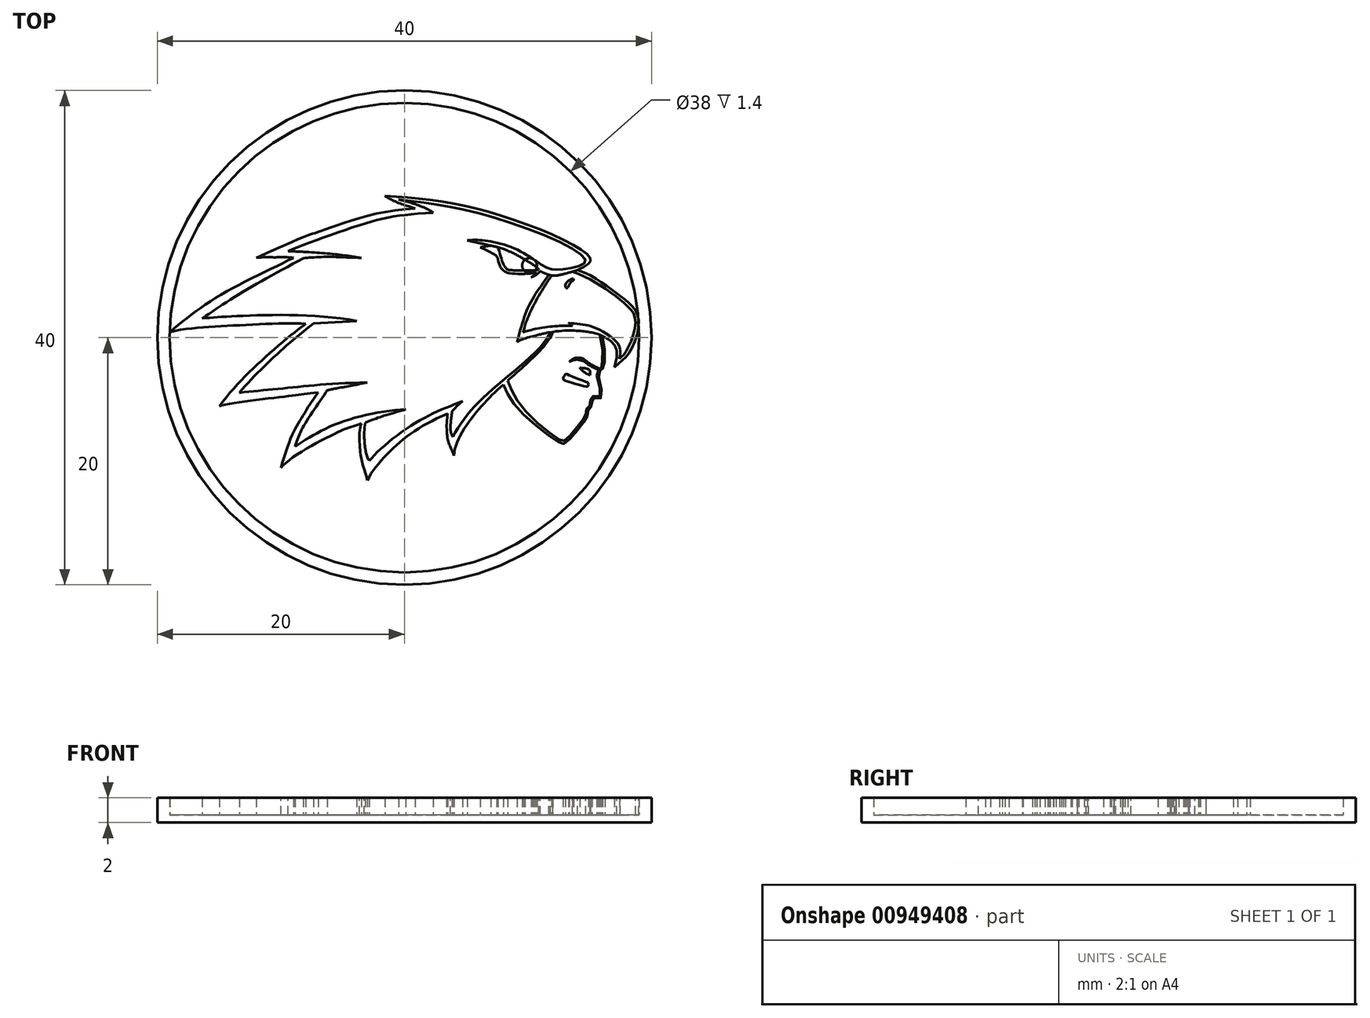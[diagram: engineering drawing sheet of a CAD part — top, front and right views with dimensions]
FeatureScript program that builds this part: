
annotation { "Feature Type Name" : "Feature", "Feature Type Description" : "" }
export const myFeature = defineFeature(function(context is Context, id is Id, definition is map)
    precondition{}
    {
        {
            var Q0;
            Q0=qCreatedBy(makeId("Top.planeOp"),FACE);
            var sketch = newSketch(context, id + "F0", { "sketchPlane" : qUnion([Q0])});
            skCircle(sketch, "E0", {"center": v(0, 0) * mm, "radius": 20 * mm});
            skSolve(sketch);
        }
        {
            var Q0;
            Q0=makeQuery(id+"F0.imprint","IMPRINT",FACE,{"disambiguationData":[TD([[makeQuery(id+"F0.imprint","IMPRINT",EDGE,{"derivedFrom":sQuery(id+"F0.wireOp",EDGE,"E0")}),1.0]])]});
            extrude(context, id + "F1", {"entities" : qUnion([Q0]), "oppositeDirection" : true, "depth" : 0.6 * mm, "offsetDistance" : 25 * mm});
        }
        {
            var Q0;
            Q0=qCreatedBy(makeId("Top.planeOp"),FACE);
            var sketch = newSketch(context, id + "F2", { "sketchPlane" : qUnion([Q0])});
            skCircle(sketch, "E1", {"center": v(0, 0) * mm, "radius": 20 * mm});
            skCircle(sketch, "E2", {"center": v(0, 0) * mm, "radius": 19 * mm});
            skSolve(sketch);
        }
        {
            var Q0;
            Q0=makeQuery(id+"F2.imprint","IMPRINT",FACE,{"disambiguationData":[TD([[makeQuery(id+"F2.imprint","IMPRINT",EDGE,{"derivedFrom":sQuery(id+"F2.wireOp",EDGE,"E1")}),1.0]])]});
            extrude(context, id + "F3", {"entities" : qUnion([Q0]), "operationType" : NewBodyOperationType.ADD, "depth" : 1.4 * mm, "offsetDistance" : 25 * mm});
        }
        {
            var Q0;
            Q0=qCreatedBy(makeId("Top.planeOp"),FACE);
            var sketch = newSketch(context, id + "F4", { "sketchPlane" : qUnion([Q0])});
            skFitSpline(sketch, "E3", {"points": [v(-1.58, 11.46) * mm, v(7.72, 9.91) * mm, v(15.05, 6.42) * mm, v(14, 5.46) * mm], "startDerivative": vector(21.52, -1.26) * mm, "endDerivative": vector(-13.3, -6.93) * mm});
            skFitSpline(sketch, "E4", {"points": [v(3.5, -6.16) * mm, v(-0.78, -8.83) * mm, v(-3, -11.54) * mm], "startDerivative": vector(-10.76, -4.46) * mm, "endDerivative": vector(-2.73, -5.76) * mm});
            skFitSpline(sketch, "E5", {"points": [v(-3, -11.54) * mm, v(-3.55, -9.5) * mm, v(-3.5, -6.96) * mm], "startDerivative": vector(-2.35, 7.78) * mm, "endDerivative": vector(1.35, 3.27) * mm});
            skFitSpline(sketch, "E6", {"points": [v(-3.5, -6.96) * mm, v(-5.27, -7.6) * mm, v(-10, -10.54) * mm], "startDerivative": vector(-9.15, -3.1) * mm, "endDerivative": vector(-2.97, -4.21) * mm});
            skFitSpline(sketch, "E7", {"points": [v(-10, -10.54) * mm, v(-8.32, -6.48) * mm, v(-7, -4.44) * mm], "startDerivative": vector(3.25, 11.93) * mm, "endDerivative": vector(2.66, 3.7) * mm});
            skFitSpline(sketch, "E8", {"points": [v(-7, -4.44) * mm, v(-9.47, -4.75) * mm, v(-15, -5.54) * mm], "startDerivative": vector(-8.24, -0.84) * mm, "endDerivative": vector(-4.12, -1.43) * mm});
            skFitSpline(sketch, "E9", {"points": [v(-15, -5.54) * mm, v(-11, -1.34) * mm, v(-8, 1.1) * mm], "startDerivative": vector(6.54, 8.64) * mm, "endDerivative": vector(3.53, 2.33) * mm});
            skFitSpline(sketch, "E10", {"points": [v(-8, 1.1) * mm, v(-13.7, 0.98) * mm, v(-19, 0.46) * mm], "startDerivative": vector(-8.4, 0.77) * mm, "endDerivative": vector(-10.04, -2.22) * mm});
            skFitSpline(sketch, "E11", {"points": [v(-19, 0.46) * mm, v(-14.13, 3.88) * mm, v(-8, 7.06) * mm], "startDerivative": vector(8.8, 7.31) * mm, "endDerivative": vector(6.6, 4.65) * mm});
            skFitSpline(sketch, "E12", {"points": [v(-12, 6.46) * mm, v(-6.88, 8.58) * mm, v(0.86, 10.46) * mm], "startDerivative": vector(30.08, 13.67) * mm, "endDerivative": vector(18.85, 0.85) * mm});
            skFitSpline(sketch, "E13", {"points": [v(0.86, 10.46) * mm, v(-0.78, 11.03) * mm, v(-1.58, 11.46) * mm], "startDerivative": vector(-2.07, 0.66) * mm, "endDerivative": vector(-0.97, 0.57) * mm});
            skFitSpline(sketch, "E14", {"points": [v(3.5, -6.16) * mm, v(3.53, -8.34) * mm, v(4, -9.54) * mm], "startDerivative": vector(-0.77, -3.97) * mm, "endDerivative": vector(1.6, -4.4) * mm});
            skFitSpline(sketch, "E15", {"points": [v(4, -9.54) * mm, v(5.91, -5.93) * mm, v(9.09, -2.82) * mm, v(12, 0.46) * mm], "startDerivative": vector(0.54, 10.48) * mm, "endDerivative": vector(2.95, 8.84) * mm});
            skFitSpline(sketch, "E16", {"points": [v(-9, 6.46) * mm, v(-10.52, 6.5) * mm, v(-12, 6.46) * mm], "startDerivative": vector(-3.14, 0.42) * mm, "endDerivative": vector(-2.86, -0.43) * mm});
            skFitSpline(sketch, "E17", {"points": [v(14, 5.46) * mm, v(16.43, 4.12) * mm, v(18.07, 2.88) * mm, v(18.94, 1.52) * mm, v(18.18, -1.26) * mm, v(17, -2.4) * mm], "startDerivative": vector(12.4, -3.48) * mm, "endDerivative": vector(-8.18, -8.07) * mm});
            skFitSpline(sketch, "E18", {"points": [v(17, -2.4) * mm, v(17.07, -0.75) * mm, v(15.73, 0.25) * mm, v(14.63, 0.5) * mm, v(12, 0.46) * mm], "startDerivative": vector(1.76, 6.26) * mm, "endDerivative": vector(-11.27, -1.86) * mm});
            skFitSpline(sketch, "E19", {"points": [v(11, 5.38) * mm, v(9.78, 6.3) * mm, v(7, 7.43) * mm], "startDerivative": vector(-2.8, 3.17) * mm, "endDerivative": vector(-5.7, 0.83) * mm});
            skFitSpline(sketch, "E20", {"points": [v(7, 7.43) * mm, v(7.74, 5.78) * mm, v(8, 5.43) * mm, v(8.44, 5.22) * mm, v(10.45, 5.2) * mm, v(10.9, 5.29) * mm, v(11, 5.38) * mm], "startDerivative": vector(6.03, -7.57) * mm, "endDerivative": vector(2.14, 2.82) * mm});
            skCircle(sketch, "E21", {"center": v(10.12, 5.84) * mm, "radius": 0.6 * mm});
            skFitSpline(sketch, "E22", {"points": [v(8, -3.8) * mm, v(9.3, -5.87) * mm, v(12.45, -8.44) * mm, v(13, -8.54) * mm, v(14.33, -7.05) * mm, v(14.82, -6.23) * mm, v(14.93, -5.76) * mm, v(15.19, -5.5) * mm, v(15.2, -4.92) * mm, v(15.93, -4.86) * mm, v(15.7, -2.86) * mm, v(15.92, -2.64) * mm, v(16.1, -2.38) * mm, v(16, 0.14) * mm], "startDerivative": vector(7.5, -17.46) * mm, "endDerivative": vector(-8.07, 26.27) * mm});
            skFitSpline(sketch, "E23", {"points": [v(15.02, -3.03) * mm, v(14.56, -2.8) * mm, v(14.2, -2.44) * mm], "startDerivative": vector(-1.12, 0.33) * mm, "endDerivative": vector(-0.33, 0.79) * mm});
            skFitSpline(sketch, "E24", {"points": [v(14.2, -2.44) * mm, v(14.57, -2.47) * mm, v(14.94, -2.61) * mm, v(15.04, -2.8) * mm, v(15.02, -3.03) * mm], "startDerivative": vector(1.37, -0.38) * mm, "endDerivative": vector(-0.15, -0.97) * mm});
            skFitSpline(sketch, "E25", {"points": [v(15.68, -2.55) * mm, v(15.48, -2.5) * mm, v(14.93, -2.22) * mm, v(14.67, -2.02) * mm, v(14.03, -1.79) * mm, v(13.34, -1.95) * mm], "startDerivative": vector(-2.24, 0.34) * mm, "endDerivative": vector(-2.61, -1.2) * mm});
            skFitSpline(sketch, "E26", {"points": [v(13.34, -1.95) * mm, v(13.86, -1.65) * mm, v(14.3, -1.65) * mm, v(14.57, -1.77) * mm, v(15.07, -2.15) * mm, v(15.55, -2.4) * mm, v(15.89, -2.49) * mm], "startDerivative": vector(2.26, 2.4) * mm, "endDerivative": vector(2.1, 0.6) * mm});
            skFitSpline(sketch, "E27", {"points": [v(15.68, -2.55) * mm, v(15.8, -2.54) * mm, v(15.89, -2.49) * mm], "startDerivative": vector(0.25, -0.06) * mm, "endDerivative": vector(0.25, 0.3) * mm});
            skFitSpline(sketch, "E28", {"points": [v(14.52, -3.93) * mm, v(12.97, -3.46) * mm, v(12.85, -3.33) * mm, v(12.9, -3.2) * mm, v(12.98, -3) * mm, v(13.07, -2.94) * mm, v(13.22, -3) * mm, v(14.68, -3.57) * mm, v(14.86, -3.66) * mm, v(14.9, -3.76) * mm, v(14.84, -3.93) * mm, v(14.78, -3.97) * mm, v(14.52, -3.93) * mm]});
            skFitSpline(sketch, "E29", {"points": [v(12, 0.46) * mm, v(10.73, 0.2) * mm, v(9.12, -0.4) * mm], "startDerivative": vector(-4.79, -0.65) * mm, "endDerivative": vector(-1.75, -1.76) * mm});
            skFitSpline(sketch, "E30", {"points": [v(9.12, -0.4) * mm, v(10.04, 2.5) * mm, v(11.7, 5.07) * mm], "startDerivative": vector(1.47, 5.98) * mm, "endDerivative": vector(3.7, 4.95) * mm});
            skFitSpline(sketch, "E31", {"points": [v(14, 5.46) * mm, v(12.41, 5.04) * mm, v(11.7, 5.07) * mm, v(11, 5.38) * mm], "startDerivative": vector(-4.1, -1.19) * mm, "endDerivative": vector(-2.43, 1.23) * mm});
            skFitSpline(sketch, "E32", {"points": [v(7, 7.43) * mm, v(5.97, 7.67) * mm, v(5.07, 7.87) * mm], "startDerivative": vector(-2.03, 0.53) * mm, "endDerivative": vector(-1.84, 0.4) * mm});
            skFitSpline(sketch, "E33", {"points": [v(5.07, 7.87) * mm, v(6.4, 7.87) * mm, v(9.35, 7) * mm, v(11.6, 5.62) * mm, v(12.86, 5.54) * mm, v(14.66, 6.18) * mm, v(7.76, 9.56) * mm, v(-0.49, 11.17) * mm], "startDerivative": vector(13.05, 0.9) * mm, "endDerivative": vector(-32.62, 3.92) * mm});
            skFitSpline(sketch, "E34", {"points": [v(-0.49, 11.17) * mm, v(0.93, 10.77) * mm, v(2.33, 10.11) * mm], "startDerivative": vector(2.94, -0.6) * mm, "endDerivative": vector(1.78, -1.4) * mm});
            skFitSpline(sketch, "E35", {"points": [v(2.33, 10.11) * mm, v(-3.07, 9.27) * mm, v(-9.44, 7) * mm], "startDerivative": vector(-15.85, -1) * mm, "endDerivative": vector(-7.4, -3.02) * mm});
            skFitSpline(sketch, "E36", {"points": [v(-9.44, 7) * mm, v(-6.18, 6.8) * mm, v(-3.48, 6.46) * mm], "startDerivative": vector(6.38, -0.27) * mm, "endDerivative": vector(5.53, -0.87) * mm});
            skFitSpline(sketch, "E37", {"points": [v(-3.48, 6.46) * mm, v(-6.21, 6.54) * mm, v(-8.18, 6.43) * mm], "startDerivative": vector(-6.33, 0.08) * mm, "endDerivative": vector(-3.05, -0.33) * mm});
            skFitSpline(sketch, "E38", {"points": [v(-8.18, 6.43) * mm, v(-13.5, 3.44) * mm, v(-16.37, 1.55) * mm], "startDerivative": vector(-9.86, -5.27) * mm, "endDerivative": vector(-6.1, -4.23) * mm});
            skFitSpline(sketch, "E39", {"points": [v(-16.37, 1.55) * mm, v(-13.5, 1.75) * mm, v(-3.85, 1.35) * mm], "startDerivative": vector(6.8, 0.6) * mm, "endDerivative": vector(14.41, -2.83) * mm});
            skFitSpline(sketch, "E40", {"points": [v(-3.85, 1.35) * mm, v(-7.35, 1.14) * mm], "startDerivative": vector(-3.5, -0.2) * mm, "endDerivative": vector(-3.5, -0.2) * mm});
            skFitSpline(sketch, "E41", {"points": [v(-7.35, 1.14) * mm, v(-10.41, -1.43) * mm, v(-13.36, -4.46) * mm], "startDerivative": vector(-6.68, -4.88) * mm, "endDerivative": vector(-5.36, -6.32) * mm});
            skFitSpline(sketch, "E42", {"points": [v(-13.36, -4.46) * mm, v(-9.36, -4.06) * mm, v(-3.02, -3.64) * mm], "startDerivative": vector(8.78, 0.94) * mm, "endDerivative": vector(14.42, 0.16) * mm});
            skFitSpline(sketch, "E43", {"points": [v(-3.02, -3.64) * mm, v(-5.54, -4.12) * mm, v(-6.24, -4.25) * mm], "startDerivative": vector(-4.48, -0.91) * mm, "endDerivative": vector(-1.64, -0.24) * mm});
            skFitSpline(sketch, "E44", {"points": [v(-6.24, -4.25) * mm, v(-8.21, -7.25) * mm, v(-8.87, -8.8) * mm], "startDerivative": vector(-3.02, -4.33) * mm, "endDerivative": vector(-1.83, -4.96) * mm});
            skFitSpline(sketch, "E45", {"points": [v(-8.87, -8.8) * mm, v(-5.6, -7.02) * mm, v(0.1, -5.81) * mm], "startDerivative": vector(6.74, 4.12) * mm, "endDerivative": vector(9.55, 0.33) * mm});
            skFitSpline(sketch, "E46", {"points": [v(0.1, -5.81) * mm, v(-1.02, -6.13) * mm, v(-3.18, -6.9) * mm], "startDerivative": vector(-4.07, -1.11) * mm, "endDerivative": vector(-5.58, -2.4) * mm});
            skFitSpline(sketch, "E47", {"points": [v(-3.18, -6.9) * mm, v(-3.14, -9.14) * mm, v(-2.84, -9.97) * mm], "startDerivative": vector(-0.7, -4.41) * mm, "endDerivative": vector(1.32, -1.52) * mm});
            skFitSpline(sketch, "E48", {"points": [v(-2.84, -9.97) * mm, v(0.78, -6.97) * mm, v(4.7, -5.14) * mm], "startDerivative": vector(3.54, 4.6) * mm, "endDerivative": vector(7.5, 2.99) * mm});
            skFitSpline(sketch, "E49", {"points": [v(4.7, -5.14) * mm, v(3.85, -5.96) * mm], "startDerivative": vector(-1.54, -1.24) * mm, "endDerivative": vector(-0.85, -0.81) * mm});
            skFitSpline(sketch, "E50", {"points": [v(3.85, -5.96) * mm, v(3.74, -7.58) * mm, v(3.91, -8.04) * mm], "startDerivative": vector(-0.38, -2.91) * mm, "endDerivative": vector(0.59, -1.08) * mm});
            skFitSpline(sketch, "E51", {"points": [v(3.91, -8.04) * mm, v(5.56, -5.69) * mm, v(8.66, -2.88) * mm, v(11.8, 0.43) * mm], "startDerivative": vector(4.66, 8.5) * mm, "endDerivative": vector(3.92, 9.27) * mm});
            skFitSpline(sketch, "E52", {"points": [v(11.8, 0.43) * mm, v(12, 0.46) * mm], "startDerivative": vector(0.2, 0.03) * mm, "endDerivative": vector(0.2, 0.03) * mm});
            skFitSpline(sketch, "E53", {"points": [v(11.92, 5.03) * mm, v(10.4, 2.5) * mm, v(9.6, 0.43) * mm], "startDerivative": vector(-3.21, -4.76) * mm, "endDerivative": vector(-1.06, -4.44) * mm});
            skFitSpline(sketch, "E54", {"points": [v(9.6, 0.43) * mm, v(10.45, 0.67) * mm, v(12.21, 0.92) * mm, v(13.6, 0.96) * mm], "startDerivative": vector(2.74, 0.91) * mm, "endDerivative": vector(3.8, 0) * mm});
            skFitSpline(sketch, "E55", {"points": [v(13.6, 0.96) * mm, v(13.29, 1.17) * mm], "startDerivative": vector(-0.45, 0.21) * mm, "endDerivative": vector(-0.45, 0.21) * mm});
            skFitSpline(sketch, "E56", {"points": [v(13.29, 1.17) * mm, v(14.52, 1.05) * mm, v(15.83, 0.62) * mm, v(17.37, -0.67) * mm, v(17.4, -1.7) * mm], "startDerivative": vector(5.3, -0.38) * mm, "endDerivative": vector(-0.98, -4.8) * mm});
            skFitSpline(sketch, "E57", {"points": [v(17.4, -1.7) * mm, v(17.94, -1.12) * mm, v(18.7, 1.36) * mm, v(18, 2.6) * mm, v(16.13, 4.03) * mm, v(13.6, 5.34) * mm], "startDerivative": vector(3.88, 3.06) * mm, "endDerivative": vector(-12.32, 4.18) * mm});
            skFitSpline(sketch, "E58", {"points": [v(7.58, 7.31) * mm, v(8.08, 5.8) * mm, v(8.4, 5.5) * mm, v(8.78, 5.45) * mm, v(10.88, 5.51) * mm], "startDerivative": vector(1.53, -5.22) * mm, "endDerivative": vector(2.76, 1.11) * mm});
            skFitSpline(sketch, "E59", {"points": [v(7.48, 6.59) * mm, v(6.84, 6.98) * mm, v(6.14, 7.3) * mm], "startDerivative": vector(-1.21, 0.84) * mm, "endDerivative": vector(-1.25, 0.39) * mm});
            skFitSpline(sketch, "E60", {"points": [v(7, 7.43) * mm, v(6.54, 7.38) * mm, v(6.14, 7.3) * mm], "startDerivative": vector(-0.92, 0.03) * mm, "endDerivative": vector(-1.04, -0.3) * mm});
            skFitSpline(sketch, "E61", {"points": [v(11, 5.38) * mm, v(10.6, 5.04) * mm, v(10.25, 4.9) * mm], "startDerivative": vector(-0.74, -0.71) * mm, "endDerivative": vector(-0.76, -0.25) * mm});
            skFitSpline(sketch, "E62", {"points": [v(10.25, 4.9) * mm, v(10.65, 5.17) * mm, v(10.88, 5.51) * mm], "startDerivative": vector(0.83, 0.5) * mm, "endDerivative": vector(0.41, 0.76) * mm});
            skFitSpline(sketch, "E63", {"points": [v(13.68, 4.76) * mm, v(13.18, 4.53) * mm, v(13.02, 4.13) * mm, v(13.16, 4) * mm, v(13.46, 4.47) * mm, v(13.69, 4.66) * mm, v(13.68, 4.76) * mm]});
            skFitSpline(sketch, "E64", {"points": [v(15.8, 0.23) * mm, v(15.96, -2.32) * mm, v(15.87, -2.55) * mm, v(15.57, -2.77) * mm, v(15.83, -4.75) * mm, v(15.14, -4.76) * mm, v(15.04, -5.45) * mm, v(14.8, -5.7) * mm, v(14.68, -6.2) * mm, v(14.23, -6.92) * mm, v(13, -8.3) * mm, v(12.54, -8.26) * mm, v(9.52, -5.66) * mm, v(8.35, -3.48) * mm], "startDerivative": vector(10.2, -30.63) * mm, "endDerivative": vector(-7.66, 17.6) * mm});
            skFitSpline(sketch, "E65", {"points": [v(10.7, 5.68) * mm, v(10.67, 6.08) * mm, v(10.45, 6.34) * mm], "startDerivative": vector(0.04, 0.82) * mm, "endDerivative": vector(-0.55, 0.49) * mm});
            skFitSpline(sketch, "E66", {"points": [v(3.5, -6.16) * mm, v(3.85, -5.96) * mm], "startDerivative": vector(0.35, 0.2) * mm, "endDerivative": vector(0.35, 0.2) * mm});
            skFitSpline(sketch, "E67", {"points": [v(-2.84, -9.97) * mm, v(-3, -11.54) * mm], "startDerivative": vector(-0.16, -1.59) * mm, "endDerivative": vector(-0.16, -1.59) * mm});
            skFitSpline(sketch, "E68", {"points": [v(-3.18, -6.9) * mm, v(-3.5, -6.96) * mm], "startDerivative": vector(-0.31, -0.06) * mm, "endDerivative": vector(-0.31, -0.06) * mm});
            skFitSpline(sketch, "E69", {"points": [v(-8.87, -8.8) * mm, v(-10, -10.54) * mm], "startDerivative": vector(-1.13, -1.75) * mm, "endDerivative": vector(-1.13, -1.75) * mm});
            skFitSpline(sketch, "E70", {"points": [v(-7, -4.44) * mm, v(-6.24, -4.25) * mm], "startDerivative": vector(0.76, 0.19) * mm, "endDerivative": vector(0.76, 0.19) * mm});
            skFitSpline(sketch, "E71", {"points": [v(-13.36, -4.46) * mm, v(-15, -5.54) * mm], "startDerivative": vector(-1.63, -1.1) * mm, "endDerivative": vector(-1.63, -1.1) * mm});
            skFitSpline(sketch, "E72", {"points": [v(-8, 1.1) * mm, v(-7.35, 1.14) * mm], "startDerivative": vector(0.65, 0.03) * mm, "endDerivative": vector(0.65, 0.03) * mm});
            skFitSpline(sketch, "E73", {"points": [v(-16.37, 1.55) * mm, v(-19, 0.46) * mm], "startDerivative": vector(-2.63, -1.1) * mm, "endDerivative": vector(-2.63, -1.1) * mm});
            skFitSpline(sketch, "E74", {"points": [v(-9, 6.46) * mm, v(-8.18, 6.43) * mm], "startDerivative": vector(0.82, -0.01) * mm, "endDerivative": vector(0.82, -0.01) * mm});
            skFitSpline(sketch, "E75", {"points": [v(-9.44, 7) * mm, v(-12, 6.46) * mm], "startDerivative": vector(-2.56, -0.56) * mm, "endDerivative": vector(-2.56, -0.56) * mm});
            skFitSpline(sketch, "E76", {"points": [v(0.86, 10.46) * mm, v(2.33, 10.11) * mm], "startDerivative": vector(1.48, -0.33) * mm, "endDerivative": vector(1.48, -0.33) * mm});
            skFitSpline(sketch, "E77", {"points": [v(-0.49, 11.17) * mm, v(-1.58, 11.46) * mm], "startDerivative": vector(-1.1, 0.27) * mm, "endDerivative": vector(-1.1, 0.27) * mm});
            skFitSpline(sketch, "E78", {"points": [v(13.6, 5.34) * mm, v(14, 5.46) * mm], "startDerivative": vector(0.4, 0.12) * mm, "endDerivative": vector(0.4, 0.12) * mm});
            skFitSpline(sketch, "E79", {"points": [v(7, 7.43) * mm, v(7.58, 7.31) * mm], "startDerivative": vector(0.57, -0.12) * mm, "endDerivative": vector(0.57, -0.12) * mm});
            skSolve(sketch);
        }
        {
            var Q0;
            {var subQ2=sQuery(id+"F4.wireOp",EDGE,"E59");Q0=makeQuery(id+"F4.imprint","IMPRINT",FACE,{"disambiguationData":[TD([[makeQuery(id+"F4.imprint","IMPRINT",EDGE,{"derivedFrom":subQ2}),-1.0]])]});}
            var Q1;
            Q1=makeQuery(id+"F4.imprint","IMPRINT",FACE,{"disambiguationData":[TD([[makeQuery(id+"F4.imprint","IMPRINT",EDGE,{"derivedFrom":sQuery(id+"F4.wireOp",EDGE,"E63")}),1.0]])]});
            var Q2;
            {var subQ0=sQuery(id+"F4.wireOp",EDGE,"E32");Q2=makeQuery(id+"F4.imprint","IMPRINT",FACE,{"disambiguationData":[TD([[makeQuery(id+"F4.imprint","IMPRINT",EDGE,{"derivedFrom":subQ0}),-1.0]])]});}
            var Q3;
            {var subQ0=sQuery(id+"F4.wireOp",EDGE,"E79");Q3=makeQuery(id+"F4.imprint","IMPRINT",FACE,{"disambiguationData":[TD([[makeQuery(id+"F4.imprint","IMPRINT",EDGE,{"derivedFrom":subQ0}),-1.0]])]});}
            var Q4;
            Q4=makeQuery(id+"F4.imprint","IMPRINT",FACE,{"disambiguationData":[TD([[makeQuery(id+"F4.imprint","IMPRINT",EDGE,{"derivedFrom":sQuery(id+"F4.wireOp",EDGE,"E3")}),-1.0]])]});
            var Q5;
            {var subQ0=sQuery(id+"F4.wireOp",EDGE,"E62");var subQ1=sQuery(id+"F4.wireOp",EDGE,"E20");var subQ2=makeQuery(id+"F4.imprint","INTERSECT",VERTEX,{"derivedFrom":[subQ1,subQ0]});Q5=makeQuery(id+"F4.imprint","IMPRINT",FACE,{"disambiguationData":[TD([[makeQuery(id+"F4.imprint","IMPRINT",EDGE,{"disambiguationData":[TD([[subQ2,-1.0]])],"derivedFrom":subQ1}),-1.0]])]});}
            var Q6;
            {var subQ1=sQuery(id+"F4.wireOp",EDGE,"E20");var subQ4=sQuery(id+"F4.wireOp",EDGE,"E62");var subQ6=makeQuery(id+"F4.imprint","INTERSECT",VERTEX,{"derivedFrom":[subQ1,subQ4]});Q6=makeQuery(id+"F4.imprint","IMPRINT",FACE,{"disambiguationData":[TD([[makeQuery(id+"F4.imprint","IMPRINT",EDGE,{"disambiguationData":[TD([[subQ6,-1.0]])],"derivedFrom":subQ1}),1.0]])]});}
            var Q7;
            {var subQ0=sQuery(id+"F4.wireOp",EDGE,"E21");var subQ1=sQuery(id+"F4.wireOp",EDGE,"E19");var subQ3=makeQuery(id+"F4.imprint","INTERSECT",VERTEX,{"derivedFrom":[subQ1,subQ0]});Q7=makeQuery(id+"F4.imprint","IMPRINT",FACE,{"disambiguationData":[TD([[makeQuery(id+"F4.imprint","IMPRINT",EDGE,{"disambiguationData":[TD([[subQ3,-1.0]])],"derivedFrom":subQ0}),1.0]])]});}
            var Q8;
            {var subQ4=sQuery(id+"F4.wireOp",EDGE,"E14");Q8=makeQuery(id+"F4.imprint","IMPRINT",FACE,{"disambiguationData":[TD([[makeQuery(id+"F4.imprint","IMPRINT",EDGE,{"derivedFrom":subQ4}),1.0]])]});}
            var Q9;
            {var subQ0=sQuery(id+"F4.wireOp",EDGE,"E22");Q9=makeQuery(id+"F4.imprint","IMPRINT",FACE,{"disambiguationData":[TD([[makeQuery(id+"F4.imprint","IMPRINT",EDGE,{"derivedFrom":subQ0}),1.0]])]});}
            var Q10;
            Q10=makeQuery(id+"F4.imprint","IMPRINT",FACE,{"disambiguationData":[TD([[makeQuery(id+"F4.imprint","IMPRINT",EDGE,{"derivedFrom":sQuery(id+"F4.wireOp",EDGE,"E23")}),-1.0]])]});
            var Q11;
            Q11=makeQuery(id+"F4.imprint","IMPRINT",FACE,{"disambiguationData":[TD([[makeQuery(id+"F4.imprint","IMPRINT",EDGE,{"derivedFrom":sQuery(id+"F4.wireOp",EDGE,"E28")}),-1.0]])]});
            var Q12;
            Q12=makeQuery(id+"F4.imprint","IMPRINT",FACE,{"disambiguationData":[TD([[makeQuery(id+"F4.imprint","IMPRINT",EDGE,{"derivedFrom":sQuery(id+"F4.wireOp",EDGE,"E25")}),-1.0]])]});
            var Q13;
            Q13=makeQuery(id+"F4.imprint","IMPRINT",FACE,{"disambiguationData":[TD([[makeQuery(id+"F4.imprint","IMPRINT",EDGE,{"derivedFrom":sQuery(id+"F4.wireOp",EDGE,"E4")}),-1.0]])]});
            var Q14;
            Q14=makeQuery(id+"F4.imprint","IMPRINT",FACE,{"disambiguationData":[TD([[makeQuery(id+"F4.imprint","IMPRINT",EDGE,{"derivedFrom":sQuery(id+"F4.wireOp",EDGE,"E5")}),-1.0]])]});
            var Q15;
            Q15=makeQuery(id+"F4.imprint","IMPRINT",FACE,{"disambiguationData":[TD([[makeQuery(id+"F4.imprint","IMPRINT",EDGE,{"derivedFrom":sQuery(id+"F4.wireOp",EDGE,"E6")}),-1.0]])]});
            var Q16;
            Q16=makeQuery(id+"F4.imprint","IMPRINT",FACE,{"disambiguationData":[TD([[makeQuery(id+"F4.imprint","IMPRINT",EDGE,{"derivedFrom":sQuery(id+"F4.wireOp",EDGE,"E7")}),-1.0]])]});
            var Q17;
            Q17=makeQuery(id+"F4.imprint","IMPRINT",FACE,{"disambiguationData":[TD([[makeQuery(id+"F4.imprint","IMPRINT",EDGE,{"derivedFrom":sQuery(id+"F4.wireOp",EDGE,"E8")}),-1.0]])]});
            var Q18;
            Q18=makeQuery(id+"F4.imprint","IMPRINT",FACE,{"disambiguationData":[TD([[makeQuery(id+"F4.imprint","IMPRINT",EDGE,{"derivedFrom":sQuery(id+"F4.wireOp",EDGE,"E9")}),-1.0]])]});
            var Q19;
            Q19=makeQuery(id+"F4.imprint","IMPRINT",FACE,{"disambiguationData":[TD([[makeQuery(id+"F4.imprint","IMPRINT",EDGE,{"derivedFrom":sQuery(id+"F4.wireOp",EDGE,"E10")}),-1.0]])]});
            var Q20;
            Q20=makeQuery(id+"F4.imprint","IMPRINT",FACE,{"disambiguationData":[TD([[makeQuery(id+"F4.imprint","IMPRINT",EDGE,{"derivedFrom":sQuery(id+"F4.wireOp",EDGE,"E11")}),-1.0]])]});
            var Q21;
            Q21=makeQuery(id+"F4.imprint","IMPRINT",FACE,{"disambiguationData":[TD([[makeQuery(id+"F4.imprint","IMPRINT",EDGE,{"derivedFrom":sQuery(id+"F4.wireOp",EDGE,"E12")}),-1.0]])]});
            var Q22;
            Q22=makeQuery(id+"F4.imprint","IMPRINT",FACE,{"disambiguationData":[TD([[makeQuery(id+"F4.imprint","IMPRINT",EDGE,{"derivedFrom":sQuery(id+"F4.wireOp",EDGE,"E13")}),-1.0]])]});
            var Q23;
            Q23=makeQuery(id+"F4.imprint","IMPRINT",FACE,{"disambiguationData":[TD([[makeQuery(id+"F4.imprint","IMPRINT",EDGE,{"derivedFrom":sQuery(id+"F4.wireOp",EDGE,"E16")}),-1.0]])]});
            extrude(context, id + "F5", {"entities" : qUnion([Q0, Q1, Q2, Q3, Q4, Q5, Q6, Q7, Q8, Q9, Q10, Q11, Q12, Q13, Q14, Q15, Q16, Q17, Q18, Q19, Q20, Q21, Q22, Q23]), "depth" : 1.4 * mm, "offsetDistance" : 25 * mm});
        }
        {
            var Q0;
            {var subQ1=sQuery(id+"F4.wireOp",EDGE,"E21");var subQ3=sQuery(id+"F4.wireOp",EDGE,"E65");var subQ8=makeQuery(id+"F4.imprint","INTERSECT",VERTEX,{"disambiguationData":[OD(1.0)],"derivedFrom":[subQ1,subQ3]});Q0=makeQuery(id+"F4.imprint","IMPRINT",FACE,{"disambiguationData":[TD([[makeQuery(id+"F4.imprint","IMPRINT",EDGE,{"disambiguationData":[TD([[subQ8,1.0]])],"derivedFrom":subQ1}),1.0]])]});}
            var Q1;
            {var subQ0=sQuery(id+"F4.wireOp",EDGE,"E58");var subQ1=sQuery(id+"F4.wireOp",EDGE,"E21");var subQ2=makeQuery(id+"F4.imprint","INTERSECT",VERTEX,{"disambiguationData":[OD(0.0)],"derivedFrom":[subQ1,subQ0]});Q1=makeQuery(id+"F4.imprint","IMPRINT",FACE,{"disambiguationData":[TD([[makeQuery(id+"F4.imprint","IMPRINT",EDGE,{"disambiguationData":[TD([[subQ2,-1.0]])],"derivedFrom":subQ1}),1.0]])]});}
            var Q2;
            {var subQ3=sQuery(id+"F4.wireOp",EDGE,"E17");Q2=makeQuery(id+"F4.imprint","IMPRINT",FACE,{"disambiguationData":[TD([[makeQuery(id+"F4.imprint","IMPRINT",EDGE,{"derivedFrom":subQ3}),-1.0]])]});}
            extrude(context, id + "F6", {"entities" : qUnion([Q0, Q1, Q2]), "depth" : 1.4 * mm, "offsetDistance" : 25 * mm});
        }
    });
